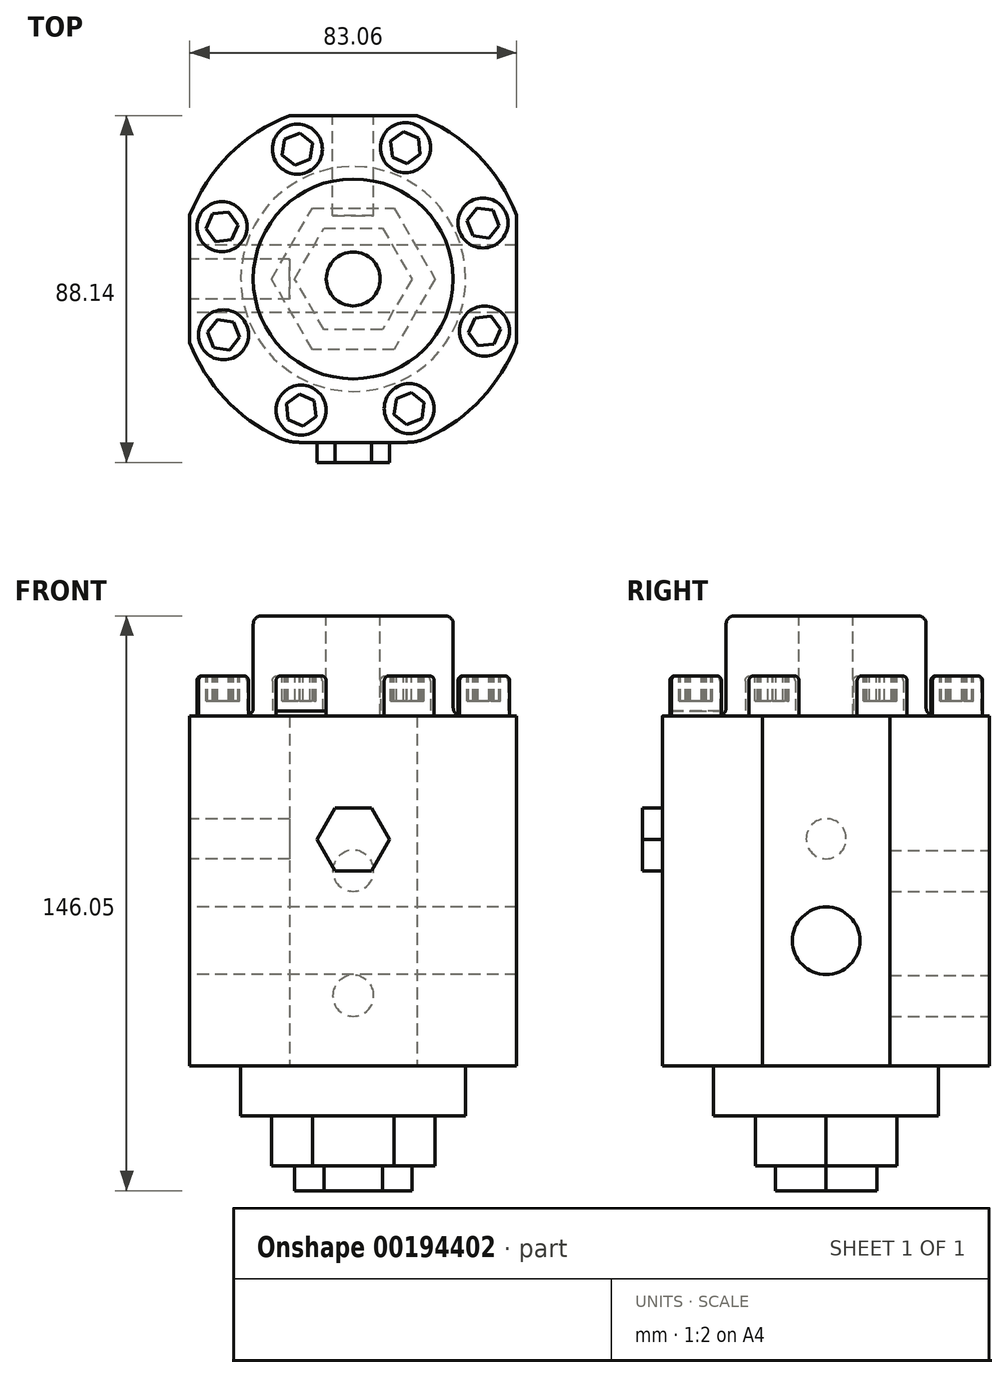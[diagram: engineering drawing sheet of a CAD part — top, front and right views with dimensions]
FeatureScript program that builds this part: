
annotation { "Feature Type Name" : "Feature", "Feature Type Description" : "" }
export const myFeature = defineFeature(function(context is Context, id is Id, definition is map)
    precondition{}
    {
        {
            var Q0;
            Q0=qCreatedBy(makeId("Top.planeOp"),FACE);
            var sketch = newSketch(context, id + "F0", { "sketchPlane" : qUnion([Q0])});
            skArc(sketch, "E0", {"start": v(41.53, 16.2) * mm, "mid": v(0, 44.58) * mm, "end": v(-41.53, 16.2) * mm});
            skLineSegment(sketch, "E1", {"start": v(41.53, 0) * mm, "end": v(41.53, 16.2) * mm});
            skLineSegment(sketch, "E2.MirrorCS", {"start": v(41.53, 0) * mm, "end": v(41.53, -16.2) * mm});
            skPoint(sketch, "E3.orphan", {"position": v(41.53, 44.35) * mm});
            skPoint(sketch, "E4.orphan", {"position": v(41.53, -44.35) * mm});
            skLineSegment(sketch, "E5.MirrorCS", {"start": v(-41.53, 0) * mm, "end": v(-41.53, -16.2) * mm});
            skLineSegment(sketch, "E6.MirrorCS", {"start": v(-41.53, 0) * mm, "end": v(-41.53, 16.2) * mm});
            skArc(sketch, "E7.trimOffspring", {"start": v(-41.53, -16.2) * mm, "mid": v(0, -44.58) * mm, "end": v(41.53, -16.2) * mm});
            skPoint(sketch, "E8.MirrorCS.end.orphan", {"position": v(-41.53, 0) * mm});
            skCircle(sketch, "E9", {"center": v(0, 0) * mm, "radius": 28.58 * mm});
            skCircle(sketch, "E10.cCircle", {"center": v(0, 0) * mm, "radius": 20.76 * mm, "construction": true});
            skLineSegment(sketch, "E10.0", {"start": v(10.38, 17.98) * mm, "end": v(20.76, 0) * mm});
            skLineSegment(sketch, "E10.1", {"start": v(20.76, 0) * mm, "end": v(10.38, -17.98) * mm});
            skLineSegment(sketch, "E10.2", {"start": v(10.38, -17.98) * mm, "end": v(-10.38, -17.98) * mm});
            skLineSegment(sketch, "E10.3", {"start": v(-10.38, -17.98) * mm, "end": v(-20.76, 0) * mm});
            skLineSegment(sketch, "E10.4", {"start": v(-20.76, 0) * mm, "end": v(-10.38, 17.98) * mm});
            skLineSegment(sketch, "E10.5", {"start": v(-10.38, 17.98) * mm, "end": v(10.38, 17.98) * mm});
            skCircle(sketch, "E11.cCircle", {"center": v(0, 0) * mm, "radius": 14.88 * mm, "construction": true});
            skLineSegment(sketch, "E11.0", {"start": v(7.44, 12.89) * mm, "end": v(14.88, 0) * mm});
            skLineSegment(sketch, "E11.1", {"start": v(14.88, 0) * mm, "end": v(7.44, -12.89) * mm});
            skLineSegment(sketch, "E11.2", {"start": v(7.44, -12.89) * mm, "end": v(-7.44, -12.89) * mm});
            skLineSegment(sketch, "E11.3", {"start": v(-7.44, -12.89) * mm, "end": v(-14.88, 0) * mm});
            skLineSegment(sketch, "E11.4", {"start": v(-14.88, 0) * mm, "end": v(-7.44, 12.89) * mm});
            skLineSegment(sketch, "E11.5", {"start": v(-7.44, 12.89) * mm, "end": v(7.44, 12.89) * mm});
            skLineSegment(sketch, "E12.1.0", {"start": v(0, -41.53) * mm, "end": v(-16.2, -41.53) * mm});
            skLineSegment(sketch, "E12.1.1", {"start": v(0, -41.53) * mm, "end": v(16.2, -41.53) * mm});
            skLineSegment(sketch, "E12.3.0", {"start": v(0, 41.53) * mm, "end": v(16.2, 41.53) * mm});
            skLineSegment(sketch, "E12.3.1", {"start": v(0, 41.53) * mm, "end": v(-16.2, 41.53) * mm});
            skSolve(sketch);
        }
        {
            var Q0;
            Q0=makeQuery(id+"F0.imprint","IMPRINT",FACE,{"disambiguationData":[TD([[makeQuery(id+"F0.imprint","IMPRINT",EDGE,{"derivedFrom":sQuery(id+"F0.wireOp",EDGE,"E0")}),1.0]])]});
            var Q1;
            Q1=makeQuery(id+"F0.imprint","IMPRINT",FACE,{"disambiguationData":[TD([[makeQuery(id+"F0.imprint","IMPRINT",EDGE,{"derivedFrom":sQuery(id+"F0.wireOp",EDGE,"E9")}),1.0]])]});
            var Q2;
            Q2=makeQuery(id+"F0.imprint","IMPRINT",FACE,{"disambiguationData":[TD([[makeQuery(id+"F0.imprint","IMPRINT",EDGE,{"derivedFrom":sQuery(id+"F0.wireOp",EDGE,"E10.0")}),-1.0]])]});
            var Q3;
            Q3=makeQuery(id+"F0.imprint","IMPRINT",FACE,{"disambiguationData":[TD([[makeQuery(id+"F0.imprint","IMPRINT",EDGE,{"derivedFrom":sQuery(id+"F0.wireOp",EDGE,"E11.0")}),-1.0]])]});
            extrude(context, id + "F1", {"entities" : qUnion([Q0, Q1, Q2, Q3]), "depth" : 88.9 * mm});
        }
        {
            var Q0;
            Q0=makeQuery(id+"F0.imprint","IMPRINT",FACE,{"disambiguationData":[TD([[makeQuery(id+"F0.imprint","IMPRINT",EDGE,{"derivedFrom":sQuery(id+"F0.wireOp",EDGE,"E9")}),1.0]])]});
            var Q1;
            Q1=makeQuery(id+"F0.imprint","IMPRINT",FACE,{"disambiguationData":[TD([[makeQuery(id+"F0.imprint","IMPRINT",EDGE,{"derivedFrom":sQuery(id+"F0.wireOp",EDGE,"E10.0")}),-1.0]])]});
            var Q2;
            Q2=makeQuery(id+"F0.imprint","IMPRINT",FACE,{"disambiguationData":[TD([[makeQuery(id+"F0.imprint","IMPRINT",EDGE,{"derivedFrom":sQuery(id+"F0.wireOp",EDGE,"E11.0")}),-1.0]])]});
            extrude(context, id + "F2", {"entities" : qUnion([Q0, Q1, Q2]), "operationType" : NewBodyOperationType.ADD, "oppositeDirection" : true, "depth" : 12.7 * mm});
        }
        {
            var Q0;
            Q0=makeQuery(id+"F0.imprint","IMPRINT",FACE,{"disambiguationData":[TD([[makeQuery(id+"F0.imprint","IMPRINT",EDGE,{"derivedFrom":sQuery(id+"F0.wireOp",EDGE,"E10.0")}),-1.0]])]});
            var Q1;
            Q1=makeQuery(id+"F0.imprint","IMPRINT",FACE,{"disambiguationData":[TD([[makeQuery(id+"F0.imprint","IMPRINT",EDGE,{"derivedFrom":sQuery(id+"F0.wireOp",EDGE,"E11.0")}),-1.0]])]});
            extrude(context, id + "F3", {"entities" : qUnion([Q0, Q1]), "operationType" : NewBodyOperationType.ADD, "oppositeDirection" : true, "depth" : 25.4 * mm});
        }
        {
            var Q0;
            Q0=makeQuery(id+"F0.imprint","IMPRINT",FACE,{"disambiguationData":[TD([[makeQuery(id+"F0.imprint","IMPRINT",EDGE,{"derivedFrom":sQuery(id+"F0.wireOp",EDGE,"E11.0")}),-1.0]])]});
            extrude(context, id + "F4", {"entities" : qUnion([Q0]), "operationType" : NewBodyOperationType.ADD, "oppositeDirection" : true, "depth" : 31.75 * mm});
        }
        {
            var Q0;
            Q0=makeQuery(id+"F4.opExtrude","CAP_FACE",FACE,{"disambiguationData":[OSD([sQuery(id+"F0.wireOp",EDGE,"E11.0"),sQuery(id+"F0.wireOp",EDGE,"E11.1"),sQuery(id+"F0.wireOp",EDGE,"E11.2"),sQuery(id+"F0.wireOp",EDGE,"E11.3"),sQuery(id+"F0.wireOp",EDGE,"E11.4"),sQuery(id+"F0.wireOp",EDGE,"E11.5")])],"isStart":false});
            cPlane(context, id + "F5", {"entities" : qUnion([Q0]), "cplaneType" : CPlaneType.OFFSET, "offset" : 63.5 * mm, "oppositeDirection" : true, "width" : 152.4 * mm, "height" : 152.4 * mm});
        }
        {
            var Q0;
            Q0=qCreatedBy(id+"F5.planeOp",FACE);
            var sketch = newSketch(context, id + "F6", { "sketchPlane" : qUnion([Q0])});
            skLineSegment(sketch, "E13", {"start": v(0, 0) * mm, "end": v(-41.53, 0) * mm});
            skSolve(sketch);
        }
        {
            var Q0;
            Q0=qCreatedBy(makeId("Front.planeOp"),FACE);
            var sketch = newSketch(context, id + "F7", { "sketchPlane" : qUnion([Q0])});
            skLineSegment(sketch, "E14", {"start": v(-41.53, 31.75) * mm, "end": v(-41.53, -2.92) * mm});
            skSolve(sketch);
        }
        {
            var Q0;
            Q0=sQuery(id+"F7.wireOp",EDGE,"E14");
            cPlane(context, id + "F8", {"entities" : qUnion([Q0]), "cplaneType" : CPlaneType.LINE_ANGLE, "offset" : 25.4 * mm, "angle" : 0 * degree, "width" : 152.4 * mm, "height" : 152.4 * mm});
        }
        {
            var Q0;
            Q0=qCreatedBy(id+"F8.planeOp",FACE);
            var sketch = newSketch(context, id + "F9", { "sketchPlane" : qUnion([Q0])});
            skCircle(sketch, "E15", {"center": v(0, 31.75) * mm, "radius": 8.57 * mm});
            skLineSegment(sketch, "E16", {"start": v(0, 31.75) * mm, "end": v(0, 57.66) * mm});
            skCircle(sketch, "E17", {"center": v(0, 57.66) * mm, "radius": 5.08 * mm});
            skSolve(sketch);
        }
        {
            var Q0;
            Q0=makeQuery(id+"F9.imprint","IMPRINT",FACE,{"disambiguationData":[TD([[makeQuery(id+"F9.imprint","IMPRINT",EDGE,{"derivedFrom":sQuery(id+"F9.wireOp",EDGE,"E15")}),1.0]])]});
            extrude(context, id + "F10", {"entities" : qUnion([Q0]), "operationType" : NewBodyOperationType.REMOVE, "oppositeDirection" : true, "depth" : 1092.2 * mm});
        }
        {
            var Q0;
            Q0=makeQuery(id+"F9.imprint","IMPRINT",FACE,{"disambiguationData":[TD([[makeQuery(id+"F9.imprint","IMPRINT",EDGE,{"derivedFrom":sQuery(id+"F9.wireOp",EDGE,"E17")}),1.0]])]});
            extrude(context, id + "F11", {"entities" : qUnion([Q0]), "operationType" : NewBodyOperationType.REMOVE, "oppositeDirection" : true, "depth" : 25.4 * mm});
        }
        {
            var Q0;
            Q0=makeQuery(id+"F1.opExtrude","CAP_FACE",FACE,{"disambiguationData":[OSD([sQuery(id+"F0.wireOp",EDGE,"E0"),sQuery(id+"F0.wireOp",EDGE,"E1"),sQuery(id+"F0.wireOp",EDGE,"E2.MirrorCS"),sQuery(id+"F0.wireOp",EDGE,"E5.MirrorCS"),sQuery(id+"F0.wireOp",EDGE,"E6.MirrorCS"),sQuery(id+"F0.wireOp",EDGE,"E7.trimOffspring")])],"isStart":false});
            var sketch = newSketch(context, id + "F12", { "sketchPlane" : qUnion([Q0])});
            skCircle(sketch, "E18", {"center": v(0, 0) * mm, "radius": 25.4 * mm});
            skSolve(sketch);
        }
        {
            var Q0;
            Q0 = qSketchRegion(id + "F12", true);
            extrude(context, id + "F13", {"entities" : qUnion([Q0]), "operationType" : NewBodyOperationType.ADD, "depth" : 25.4 * mm});
        }
        {
            var Q0;
            Q0=makeQuery(id+"F13.opExtrude","SWEPT_FACE",FACE,{"disambiguationData":[OSD([sQuery(id+"F12.wireOp",EDGE,"E18")])]});
            fillet(context, id + "F14", {"entities" : qUnion([Q0]), "radius" : 2.03 * mm, "tangentPropagation" : true, "allowEdgeOverflow" : false});
        }
        {
            var Q0;
            Q0=makeQuery(id+"F1.opExtrude","SWEPT_FACE",FACE,{"disambiguationData":[OSD([sQuery(id+"F0.wireOp",EDGE,"E12.1.0"),sQuery(id+"F0.wireOp",EDGE,"E12.1.1")])]});
            var sketch = newSketch(context, id + "F15", { "sketchPlane" : qUnion([Q0])});
            skLineSegment(sketch, "E19", {"start": v(0, 88.9) * mm, "end": v(0, 57.48) * mm});
            skPoint(sketch, "E19.endSnap0", {"position": v(0, 88.9) * mm});
            skCircle(sketch, "E20.cCircle", {"center": v(0, 57.48) * mm, "radius": 9.18 * mm, "construction": true});
            skLineSegment(sketch, "E20.0", {"start": v(4.6, 49.53) * mm, "end": v(-4.6, 49.53) * mm});
            skLineSegment(sketch, "E20.1", {"start": v(-4.6, 49.53) * mm, "end": v(-9.18, 57.48) * mm});
            skLineSegment(sketch, "E20.2", {"start": v(-9.18, 57.48) * mm, "end": v(-4.6, 65.43) * mm});
            skLineSegment(sketch, "E20.3", {"start": v(-4.6, 65.43) * mm, "end": v(4.6, 65.43) * mm});
            skLineSegment(sketch, "E20.4", {"start": v(4.6, 65.43) * mm, "end": v(9.18, 57.48) * mm});
            skLineSegment(sketch, "E20.5", {"start": v(9.18, 57.48) * mm, "end": v(4.6, 49.53) * mm});
            skSolve(sketch);
        }
        {
            var Q0;
            Q0 = qSketchRegion(id + "F15", true);
            extrude(context, id + "F16", {"entities" : qUnion([Q0]), "operationType" : NewBodyOperationType.ADD, "depth" : 5.08 * mm});
        }
        {
            var Q0;
            Q0=makeQuery(id+"F13.opExtrude","CAP_FACE",FACE,{"disambiguationData":[OSD([sQuery(id+"F12.wireOp",EDGE,"E18")])],"isStart":false});
            var sketch = newSketch(context, id + "F17", { "sketchPlane" : qUnion([Q0])});
            skCircle(sketch, "E21", {"center": v(0, 0) * mm, "radius": 6.86 * mm});
            skSolve(sketch);
        }
        {
            var Q0;
            Q0 = qSketchRegion(id + "F17", true);
            extrude(context, id + "F18", {"entities" : qUnion([Q0]), "operationType" : NewBodyOperationType.REMOVE, "oppositeDirection" : true, "depth" : 25.4 * mm});
        }
        {
            var Q0;
            Q0=makeQuery(id+"F1.opExtrude","SWEPT_FACE",FACE,{"disambiguationData":[OSD([sQuery(id+"F0.wireOp",EDGE,"E12.3.0"),sQuery(id+"F0.wireOp",EDGE,"E12.3.1")])]});
            var sketch = newSketch(context, id + "F19", { "sketchPlane" : qUnion([Q0])});
            skLineSegment(sketch, "E22", {"start": v(0, 0) * mm, "end": v(0, 17.78) * mm});
            skCircle(sketch, "E23", {"center": v(0, 17.78) * mm, "radius": 5.2 * mm});
            skLineSegment(sketch, "E24", {"start": v(0, 17.78) * mm, "end": v(0, 49.53) * mm});
            skCircle(sketch, "E25", {"center": v(0, 49.53) * mm, "radius": 5.2 * mm});
            skSolve(sketch);
        }
        {
            var Q0;
            Q0=makeQuery(id+"F19.imprint","IMPRINT",FACE,{"disambiguationData":[TD([[makeQuery(id+"F19.imprint","IMPRINT",EDGE,{"derivedFrom":sQuery(id+"F19.wireOp",EDGE,"E25")}),1.0]])]});
            var Q1;
            {var subQ0=sQuery(id+"F19.wireOp",EDGE,"E24");var subQ1=sQuery(id+"F19.wireOp",EDGE,"E22");var subQ2=makeQuery(id+"F19.imprint","INTERSECT",VERTEX,{"derivedFrom":[subQ1,subQ0]});Q1=makeQuery(id+"F19.imprint","IMPRINT",FACE,{"disambiguationData":[TD([[makeQuery(id+"F19.imprint","IMPRINT",EDGE,{"disambiguationData":[TD([[subQ2,1.0]])],"derivedFrom":subQ1}),-1.0]])]});}
            var Q2;
            {var subQ0=sQuery(id+"F19.wireOp",EDGE,"E24");var subQ1=sQuery(id+"F19.wireOp",EDGE,"E22");var subQ2=makeQuery(id+"F19.imprint","INTERSECT",VERTEX,{"derivedFrom":[subQ1,subQ0]});Q2=makeQuery(id+"F19.imprint","IMPRINT",FACE,{"disambiguationData":[TD([[makeQuery(id+"F19.imprint","IMPRINT",EDGE,{"disambiguationData":[TD([[subQ2,1.0]])],"derivedFrom":subQ1}),1.0]])]});}
            extrude(context, id + "F20", {"entities" : qUnion([Q0, Q1, Q2]), "operationType" : NewBodyOperationType.REMOVE, "oppositeDirection" : true, "depth" : 25.4 * mm});
        }
        {
            var Q0;
            Q0=makeQuery(id+"F1.opExtrude","SWEPT_EDGE",EDGE,{"disambiguationData":[OSD([sQuery(id+"F0.wireOp",EDGE,"E7.trimOffspring"),sQuery(id+"F0.wireOp",EDGE,"E12.1.0")])]});
            var Q1;
            Q1=makeQuery(id+"F1.opExtrude","SWEPT_EDGE",EDGE,{"disambiguationData":[OSD([sQuery(id+"F0.wireOp",EDGE,"E7.trimOffspring"),sQuery(id+"F0.wireOp",EDGE,"E12.1.1")])]});
            fillet(context, id + "F21", {"entities" : qUnion([Q0, Q1]), "radius" : 12.7 * mm, "tangentPropagation" : true, "allowEdgeOverflow" : false});
        }
        {
            var Q0;
            Q0=makeQuery(id+"F1.opExtrude","CAP_FACE",FACE,{"disambiguationData":[OSD([sQuery(id+"F0.wireOp",EDGE,"E0"),sQuery(id+"F0.wireOp",EDGE,"E5.MirrorCS"),sQuery(id+"F0.wireOp",EDGE,"E6.MirrorCS"),sQuery(id+"F0.wireOp",EDGE,"E7.trimOffspring"),sQuery(id+"F0.wireOp",EDGE,"E12.1.0"),sQuery(id+"F0.wireOp",EDGE,"E12.1.1"),sQuery(id+"F0.wireOp",EDGE,"E2.MirrorCS"),sQuery(id+"F0.wireOp",EDGE,"E1"),sQuery(id+"F0.wireOp",EDGE,"E12.3.0"),sQuery(id+"F0.wireOp",EDGE,"E12.3.1")])],"isStart":false});
            var sketch = newSketch(context, id + "F22", { "sketchPlane" : qUnion([Q0])});
            skLineSegment(sketch, "E26", {"start": v(0, 0) * mm, "end": v(-16.38, -41.22) * mm});
            skLineSegment(sketch, "E27", {"start": v(-16.38, -41.22) * mm, "end": v(-10.13, -25.5) * mm});
            skLineSegment(sketch, "E28", {"start": v(-10.13, -25.5) * mm, "end": v(-13.25, -33.36) * mm});
            skCircle(sketch, "E29", {"center": v(-13.25, -33.36) * mm, "radius": 6.35 * mm});
            skCircle(sketch, "E30", {"center": v(-13.25, -33.36) * mm, "radius": 7.94 * mm});
            skCircle(sketch, "E31.cCircle", {"center": v(-13.25, -33.36) * mm, "radius": 3.96 * mm, "construction": true});
            skLineSegment(sketch, "E31.0", {"start": v(-10.15, -30.9) * mm, "end": v(-9.57, -34.82) * mm});
            skLineSegment(sketch, "E31.1", {"start": v(-9.57, -34.82) * mm, "end": v(-12.68, -37.28) * mm});
            skLineSegment(sketch, "E31.2", {"start": v(-12.68, -37.28) * mm, "end": v(-16.36, -35.81) * mm});
            skLineSegment(sketch, "E31.3", {"start": v(-16.36, -35.81) * mm, "end": v(-16.93, -31.9) * mm});
            skLineSegment(sketch, "E31.4", {"start": v(-16.93, -31.9) * mm, "end": v(-13.83, -29.44) * mm});
            skLineSegment(sketch, "E31.5", {"start": v(-13.83, -29.44) * mm, "end": v(-10.15, -30.9) * mm});
            skSolve(sketch);
        }
        {
            var Q0;
            {var subQ0=sQuery(id+"F22.wireOp",EDGE,"E30");var subQ1=sQuery(id+"F22.wireOp",EDGE,"E27");var subQ2=makeQuery(id+"F22.imprint","INTERSECT",VERTEX,{"derivedFrom":[subQ1,subQ0]});Q0=makeQuery(id+"F22.imprint","IMPRINT",FACE,{"disambiguationData":[TD([[makeQuery(id+"F22.imprint","IMPRINT",EDGE,{"disambiguationData":[TD([[subQ2,-1.0]])],"derivedFrom":subQ1}),-1.0]])]});}
            var Q1;
            {var subQ0=sQuery(id+"F22.wireOp",EDGE,"E30");var subQ1=sQuery(id+"F22.wireOp",EDGE,"E27");var subQ2=makeQuery(id+"F22.imprint","INTERSECT",VERTEX,{"derivedFrom":[subQ1,subQ0]});Q1=makeQuery(id+"F22.imprint","IMPRINT",FACE,{"disambiguationData":[TD([[makeQuery(id+"F22.imprint","IMPRINT",EDGE,{"disambiguationData":[TD([[subQ2,-1.0]])],"derivedFrom":subQ1}),1.0]])]});}
            var Q2;
            {var subQ0=sQuery(id+"F22.wireOp",EDGE,"E31.3");Q2=makeQuery(id+"F22.imprint","IMPRINT",FACE,{"disambiguationData":[TD([[makeQuery(id+"F22.imprint","IMPRINT",EDGE,{"derivedFrom":subQ0}),1.0]])]});}
            var Q3;
            {var subQ0=sQuery(id+"F22.wireOp",EDGE,"E31.0");Q3=makeQuery(id+"F22.imprint","IMPRINT",FACE,{"disambiguationData":[TD([[makeQuery(id+"F22.imprint","IMPRINT",EDGE,{"derivedFrom":subQ0}),1.0]])]});}
            var Q4;
            {var subQ6=sQuery(id+"F22.wireOp",EDGE,"E31.0");Q4=makeQuery(id+"F22.imprint","IMPRINT",FACE,{"disambiguationData":[TD([[makeQuery(id+"F22.imprint","IMPRINT",EDGE,{"derivedFrom":subQ6}),-1.0]])]});}
            var Q5;
            {var subQ0=sQuery(id+"F22.wireOp",EDGE,"E31.3");Q5=makeQuery(id+"F22.imprint","IMPRINT",FACE,{"disambiguationData":[TD([[makeQuery(id+"F22.imprint","IMPRINT",EDGE,{"derivedFrom":subQ0}),-1.0]])]});}
            extrude(context, id + "F23", {"entities" : qUnion([Q0, Q1, Q2, Q3, Q4, Q5]), "depth" : 1.27 * mm});
        }
        {
            var Q0;
            {var subQ0=sQuery(id+"F22.wireOp",EDGE,"E31.3");Q0=makeQuery(id+"F22.imprint","IMPRINT",FACE,{"disambiguationData":[TD([[makeQuery(id+"F22.imprint","IMPRINT",EDGE,{"derivedFrom":subQ0}),1.0]])]});}
            var Q1;
            {var subQ0=sQuery(id+"F22.wireOp",EDGE,"E31.0");Q1=makeQuery(id+"F22.imprint","IMPRINT",FACE,{"disambiguationData":[TD([[makeQuery(id+"F22.imprint","IMPRINT",EDGE,{"derivedFrom":subQ0}),1.0]])]});}
            var Q2;
            {var subQ0=sQuery(id+"F22.wireOp",EDGE,"E31.3");Q2=makeQuery(id+"F22.imprint","IMPRINT",FACE,{"disambiguationData":[TD([[makeQuery(id+"F22.imprint","IMPRINT",EDGE,{"derivedFrom":subQ0}),-1.0]])]});}
            var Q3;
            {var subQ6=sQuery(id+"F22.wireOp",EDGE,"E31.0");Q3=makeQuery(id+"F22.imprint","IMPRINT",FACE,{"disambiguationData":[TD([[makeQuery(id+"F22.imprint","IMPRINT",EDGE,{"derivedFrom":subQ6}),-1.0]])]});}
            extrude(context, id + "F24", {"entities" : qUnion([Q0, Q1, Q2, Q3]), "depth" : 10.16 * mm});
        }
        {
            var Q0;
            Q0=makeQuery(id+"F24.opExtrude","CAP_FACE",FACE,{"disambiguationData":[OSD([sQuery(id+"F22.wireOp",EDGE,"E29")])],"isStart":false});
            var sketch = newSketch(context, id + "F25", { "sketchPlane" : qUnion([Q0])});
            skCircle(sketch, "E32.cCircle", {"center": v(-13.25, -33.36) * mm, "radius": 4.1 * mm, "construction": true});
            skLineSegment(sketch, "E32.0", {"start": v(-9.95, -30.94) * mm, "end": v(-9.5, -35.01) * mm});
            skLineSegment(sketch, "E32.1", {"start": v(-9.5, -35.01) * mm, "end": v(-12.82, -37.43) * mm});
            skLineSegment(sketch, "E32.2", {"start": v(-12.82, -37.43) * mm, "end": v(-16.56, -35.77) * mm});
            skLineSegment(sketch, "E32.3", {"start": v(-16.56, -35.77) * mm, "end": v(-17, -31.7) * mm});
            skLineSegment(sketch, "E32.4", {"start": v(-17, -31.7) * mm, "end": v(-13.7, -29.29) * mm});
            skLineSegment(sketch, "E32.5", {"start": v(-13.7, -29.29) * mm, "end": v(-9.95, -30.94) * mm});
            skSolve(sketch);
        }
        {
            var Q0;
            Q0 = qSketchRegion(id + "F25", true);
            extrude(context, id + "F26", {"entities" : qUnion([Q0]), "operationType" : NewBodyOperationType.REMOVE, "oppositeDirection" : true, "depth" : 6.35 * mm});
        }
        {
            var Q0;
            Q0=makeQuery(id+"F24.opExtrude","CAP_EDGE",EDGE,{"disambiguationData":[OSD([sQuery(id+"F22.wireOp",EDGE,"E29")])],"isStart":false});
            fillet(context, id + "F27", {"entities" : qUnion([Q0]), "radius" : 1.27 * mm, "tangentPropagation" : true, "allowEdgeOverflow" : false});
        }
        {
            var Q0;
            Q0=makeQuery(id+"F24.opExtrude","SWEPT_BODY",BODY,{"disambiguationData":[OSD([sQuery(id+"F22.wireOp",EDGE,"E29")])]});
            var Q1;
            Q1=makeQuery(id+"F23.opExtrude","SWEPT_BODY",BODY,{"disambiguationData":[OSD([sQuery(id+"F22.wireOp",EDGE,"E30")])]});
            var Q2;
            Q2=makeQuery(id+"F18.boolean.opBoolean","COPY",FACE,{"derivedFrom":makeQuery(id+"F18.opExtrude","SWEPT_FACE",FACE,{"disambiguationData":[OSD([sQuery(id+"F17.wireOp",EDGE,"E21")])]})});
            circularPattern(context, id + "F28", {"entities" : qUnion([Q0, Q1]), "axis" : qUnion([Q2]), "angle" : 360 * degree, "instanceCount" : 8, "equalSpace" : true});
        }
    });
